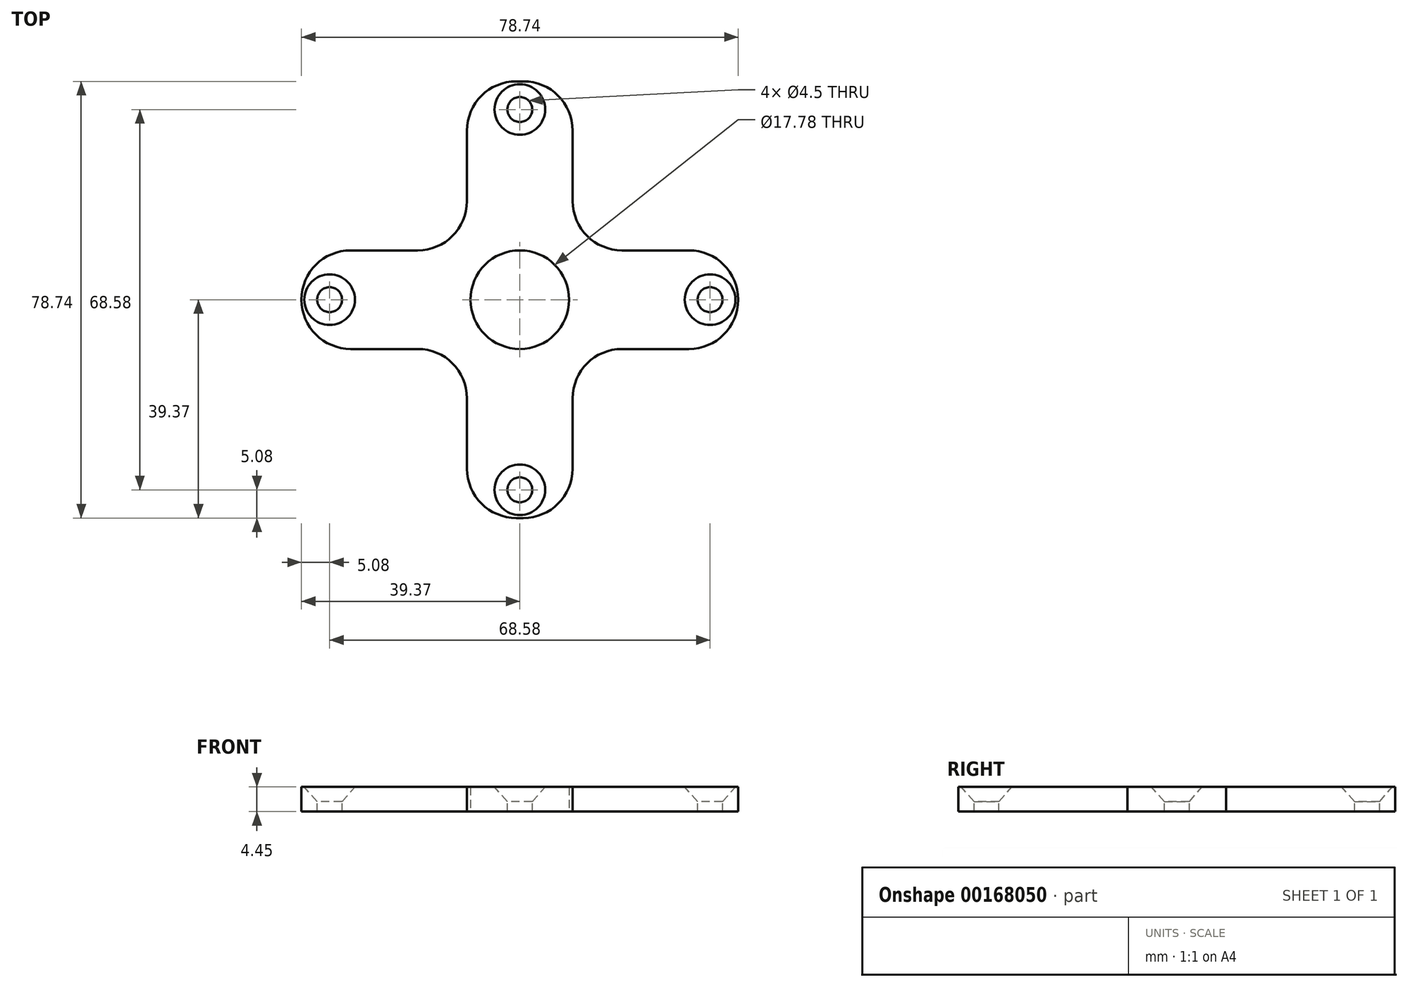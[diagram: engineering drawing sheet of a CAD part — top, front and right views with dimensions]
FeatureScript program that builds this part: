
annotation { "Feature Type Name" : "Feature", "Feature Type Description" : "" }
export const myFeature = defineFeature(function(context is Context, id is Id, definition is map)
    precondition{}
    {
        {
            var Q0;
            Q0=qCreatedBy(makeId("Top.planeOp"),FACE);
            var sketch = newSketch(context, id + "F0", { "sketchPlane" : qUnion([Q0])});
            skLineSegment(sketch, "E0.bottom", {"start": v(39.37, -8.89) * mm, "end": v(-39.37, -8.9) * mm});
            skLineSegment(sketch, "E0.top", {"start": v(39.37, 8.9) * mm, "end": v(-39.37, 8.9) * mm});
            skLineSegment(sketch, "E0.left", {"start": v(39.37, -8.89) * mm, "end": v(39.37, 8.9) * mm});
            skLineSegment(sketch, "E0.right", {"start": v(-39.37, -8.9) * mm, "end": v(-39.37, 8.9) * mm});
            skPoint(sketch, "E0.middle", {"position": v(0, 0) * mm});
            skSolve(sketch);
        }
        {
            var Q0;
            Q0 = qSketchRegion(id + "F0", true);
            extrude(context, id + "F1", {"entities" : qUnion([Q0]), "depth" : 4.44 * mm});
        }
        {
            var Q0;
            Q0=qCreatedBy(makeId("Top.planeOp"),FACE);
            var sketch = newSketch(context, id + "F2", { "sketchPlane" : qUnion([Q0])});
            skLineSegment(sketch, "E1.bottom", {"start": v(9.52, -39.37) * mm, "end": v(-9.53, -39.37) * mm});
            skLineSegment(sketch, "E1.top", {"start": v(9.53, 39.37) * mm, "end": v(-9.52, 39.37) * mm});
            skLineSegment(sketch, "E1.left", {"start": v(9.52, -39.37) * mm, "end": v(9.53, 39.37) * mm});
            skLineSegment(sketch, "E1.right", {"start": v(-9.53, -39.37) * mm, "end": v(-9.53, 39.37) * mm});
            skPoint(sketch, "E1.middle", {"position": v(0, 0) * mm});
            skSolve(sketch);
        }
        {
            var Q0;
            Q0 = qSketchRegion(id + "F2", true);
            var Q1;
            Q1=makeQuery(id+"F1.opExtrude","CAP_FACE",FACE,{"disambiguationData":[OSD([sQuery(id+"F0.wireOp",EDGE,"E0.bottom"),sQuery(id+"F0.wireOp",EDGE,"E0.top"),sQuery(id+"F0.wireOp",EDGE,"E0.left"),sQuery(id+"F0.wireOp",EDGE,"E0.right")])],"isStart":false});
            extrude(context, id + "F3", {"entities" : qUnion([Q0]), "operationType" : NewBodyOperationType.ADD, "endBound" : BoundingType.UP_TO_SURFACE, "endBoundEntityFace" : qUnion([Q1]), "depth" : 25.4 * mm});
        }
        {
            var Q0;
            Q0=makeQuery(id+"F3.opExtrude","SWEPT_EDGE",EDGE,{"disambiguationData":[OSD([sQuery(id+"F2.wireOp",EDGE,"E1.bottom"),sQuery(id+"F2.wireOp",EDGE,"E1.left")])]});
            var Q1;
            Q1=makeQuery(id+"F3.opExtrude","SWEPT_EDGE",EDGE,{"disambiguationData":[OSD([sQuery(id+"F2.wireOp",EDGE,"E1.bottom"),sQuery(id+"F2.wireOp",EDGE,"E1.right")])]});
            var Q2;
            Q2=makeQuery(id+"F1.opExtrude","SWEPT_EDGE",EDGE,{"disambiguationData":[OSD([sQuery(id+"F0.wireOp",EDGE,"E0.bottom"),sQuery(id+"F0.wireOp",EDGE,"E0.left")])]});
            var Q3;
            Q3=makeQuery(id+"F1.opExtrude","SWEPT_EDGE",EDGE,{"disambiguationData":[OSD([sQuery(id+"F0.wireOp",EDGE,"E0.top"),sQuery(id+"F0.wireOp",EDGE,"E0.left")])]});
            var Q4;
            Q4=makeQuery(id+"F3.opExtrude","SWEPT_EDGE",EDGE,{"disambiguationData":[OSD([sQuery(id+"F2.wireOp",EDGE,"E1.top"),sQuery(id+"F2.wireOp",EDGE,"E1.left")])]});
            var Q5;
            Q5=makeQuery(id+"F1.opExtrude","SWEPT_EDGE",EDGE,{"disambiguationData":[OSD([sQuery(id+"F0.wireOp",EDGE,"E0.bottom"),sQuery(id+"F0.wireOp",EDGE,"E0.right")])]});
            var Q6;
            Q6=makeQuery(id+"F1.opExtrude","SWEPT_EDGE",EDGE,{"disambiguationData":[OSD([sQuery(id+"F0.wireOp",EDGE,"E0.top"),sQuery(id+"F0.wireOp",EDGE,"E0.right")])]});
            var Q7;
            Q7=makeQuery(id+"F3.boolean.opBoolean","INTERSECT",EDGE,{"derivedFrom":[makeQuery(id+"F1.opExtrude","SWEPT_FACE",FACE,{"disambiguationData":[OSD([sQuery(id+"F0.wireOp",EDGE,"E0.top")])]}),makeQuery(id+"F3.opExtrude","SWEPT_FACE",FACE,{"disambiguationData":[OSD([sQuery(id+"F2.wireOp",EDGE,"E1.right")])]})]});
            var Q8;
            Q8=makeQuery(id+"F3.opExtrude","SWEPT_EDGE",EDGE,{"disambiguationData":[OSD([sQuery(id+"F2.wireOp",EDGE,"E1.top"),sQuery(id+"F2.wireOp",EDGE,"E1.right")])]});
            var Q9;
            Q9=makeQuery(id+"F3.boolean.opBoolean","INTERSECT",EDGE,{"derivedFrom":[makeQuery(id+"F1.opExtrude","SWEPT_FACE",FACE,{"disambiguationData":[OSD([sQuery(id+"F0.wireOp",EDGE,"E0.bottom")])]}),makeQuery(id+"F3.opExtrude","SWEPT_FACE",FACE,{"disambiguationData":[OSD([sQuery(id+"F2.wireOp",EDGE,"E1.right")])]})]});
            var Q10;
            Q10=makeQuery(id+"F3.boolean.opBoolean","INTERSECT",EDGE,{"derivedFrom":[makeQuery(id+"F1.opExtrude","SWEPT_FACE",FACE,{"disambiguationData":[OSD([sQuery(id+"F0.wireOp",EDGE,"E0.bottom")])]}),makeQuery(id+"F3.opExtrude","SWEPT_FACE",FACE,{"disambiguationData":[OSD([sQuery(id+"F2.wireOp",EDGE,"E1.left")])]})]});
            var Q11;
            Q11=makeQuery(id+"F3.boolean.opBoolean","INTERSECT",EDGE,{"derivedFrom":[makeQuery(id+"F1.opExtrude","SWEPT_FACE",FACE,{"disambiguationData":[OSD([sQuery(id+"F0.wireOp",EDGE,"E0.top")])]}),makeQuery(id+"F3.opExtrude","SWEPT_FACE",FACE,{"disambiguationData":[OSD([sQuery(id+"F2.wireOp",EDGE,"E1.left")])]})]});
            fillet(context, id + "F4", {"entities" : qUnion([Q0, Q1, Q2, Q3, Q4, Q5, Q6, Q7, Q8, Q9, Q10, Q11]), "radius" : 8.9 * mm, "tangentPropagation" : true, "allowEdgeOverflow" : false});
        }
        {
            var Q0;
            Q0=makeQuery(id+"F3.boolean.opBoolean","MERGE",FACE,{"derivedFrom":[makeQuery(id+"F1.opExtrude","CAP_FACE",FACE,{"disambiguationData":[OSD([sQuery(id+"F0.wireOp",EDGE,"E0.bottom"),sQuery(id+"F0.wireOp",EDGE,"E0.top"),sQuery(id+"F0.wireOp",EDGE,"E0.left"),sQuery(id+"F0.wireOp",EDGE,"E0.right")])],"isStart":false}),makeQuery(id+"F3.opExtrude","CAP_FACE",FACE,{"disambiguationData":[OSD([sQuery(id+"F2.wireOp",EDGE,"E1.bottom"),sQuery(id+"F2.wireOp",EDGE,"E1.top"),sQuery(id+"F2.wireOp",EDGE,"E1.left"),sQuery(id+"F2.wireOp",EDGE,"E1.right")])],"isStart":false})]});
            var sketch = newSketch(context, id + "F5", { "sketchPlane" : qUnion([Q0])});
            skPoint(sketch, "E2", {"position": v(34.3, 0) * mm});
            skLineSegment(sketch, "E3", {"start": v(0, 0) * mm, "end": v(34.29, 0) * mm, "construction": true});
            skPoint(sketch, "E4.1.0", {"position": v(0, 34.3) * mm});
            skPoint(sketch, "E4.2.0", {"position": v(-34.3, 0) * mm});
            skPoint(sketch, "E4.3.0", {"position": v(0, -34.3) * mm});
            skPoint(sketch, "E4.center", {"position": v(0, 0) * mm});
            skSolve(sketch);
        }
        {
            var Q0;
            Q0=sQuery(id+"F5.wireOp",VERTEX,"E2");
            var Q1;
            Q1=sQuery(id+"F5.wireOp",VERTEX,"E4.3.0");
            var Q2;
            Q2=sQuery(id+"F5.wireOp",VERTEX,"E4.2.0");
            var Q3;
            Q3=sQuery(id+"F5.wireOp",VERTEX,"E4.1.0");
            var Q4;
            Q4=makeQuery(id+"F1.opExtrude","SWEPT_BODY",BODY,{"disambiguationData":[OSD([sQuery(id+"F0.wireOp",EDGE,"E0.bottom"),sQuery(id+"F0.wireOp",EDGE,"E0.top"),sQuery(id+"F0.wireOp",EDGE,"E0.left"),sQuery(id+"F0.wireOp",EDGE,"E0.right")])]});
            hole(context, id + "F6", {"style" : HoleStyle.C_SINK, "endStyle" : HoleEndStyle.THROUGH, "standardTappedOrClearance" : lookupTablePath({ "standard" : "ANSI", "fit" : "Normal (ASME)", "size" : "#8", "type" : "Clearance" }), "standardBlindInLast" : lookupTablePath({ "fit" : "Free", "standard" : "ANSI", "size" : "#8", "type" : "Clearance" }), "holeDiameter" : 4.5 * mm, "cSinkDiameter" : 9.12 * mm, "cSinkAngle" : 82 * degree, "locations" : qUnion([Q0, Q1, Q2, Q3]), "scope" : qUnion([Q4]), "isTappedThrough" : true});
        }
        {
            var Q0;
            Q0=qCreatedBy(makeId("Top.planeOp"),FACE);
            var sketch = newSketch(context, id + "F7", { "sketchPlane" : qUnion([Q0])});
            skCircle(sketch, "E5", {"center": v(0, 0) * mm, "radius": 8.9 * mm});
            skSolve(sketch);
        }
        {
            var Q0;
            Q0=makeQuery(id+"F7.imprint","IMPRINT",FACE,{"disambiguationData":[TD([[makeQuery(id+"F7.imprint","IMPRINT",EDGE,{"derivedFrom":sQuery(id+"F7.wireOp",EDGE,"E5")}),1.0]])]});
            extrude(context, id + "F8", {"entities" : qUnion([Q0]), "operationType" : NewBodyOperationType.REMOVE, "endBound" : BoundingType.THROUGH_ALL, "depth" : 25.4 * mm});
        }
    });
